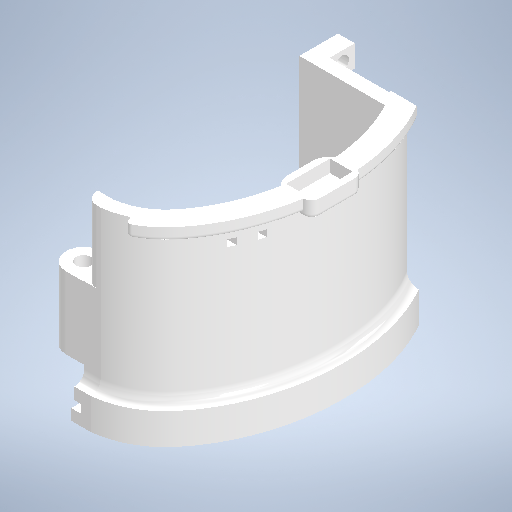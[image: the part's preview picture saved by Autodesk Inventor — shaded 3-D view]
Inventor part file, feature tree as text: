
AUTODESK INVENTOR PART (.ipt)
format: ipt  version: 2025.2 (Build 292293000, 293)  size: 573,952 bytes
history: native  units: in
note: dims shown in document units (in); Inventor stores cm internally (conversion verified against a paired STEP export)
features: fillet x6, other x3, extrude x2, sketch x2, reference x1
ambient origin geometry x8: Origin, YZ Plane, XZ Plane, XY Plane, X Axis, Y Axis, Z Axis, Center Point
bodies: Solid1 (feature_tree), Body1 (feature_tree)
feature tree (14):
  extrude  "Extrusion3"  Depth=0.1693in
  extrude  "Extrusion4"  Depth=0.0787in TaperAngle=0.0deg
  fillet  "Fillet13"  Radius=0.1063in
  fillet  "Fillet14"  Radius=0.2047in
  fillet  "Fillet15"  Radius=0.0591in
  fillet  "Fillet16"  Radius=0.0394in
  fillet  "Fillet17"  Radius=0.0394in
  fillet  "Fillet18"  Radius=0.0213in
  sketch  "Sketch3"  dims[d29=90.0deg d30=0.1693in]
  reference  "Reference1"
  sketch  "Sketch4"  dims[d31=0.2441in d32=0.0787in d33=0.0in d34=0.1063in d35=0.2047in d36=0.0591in d37=0.0in d38=0.0394in d39=0.0394in d40=0.0213in d41=0.0787in d42=0.0787in d43=0.0197in d18=0.0in d19=0.0in d20=0.0in d21=0.0in d22=0.0in d23=0.0in]
  other  "<userpath>\Downloads\rat_cap_EC_v12 v0\rat_cap_walls_v8.iam"
  other  "rat_cap_walls_v8.iam"
  other  "rat_cap_left_wall_v8:1"
